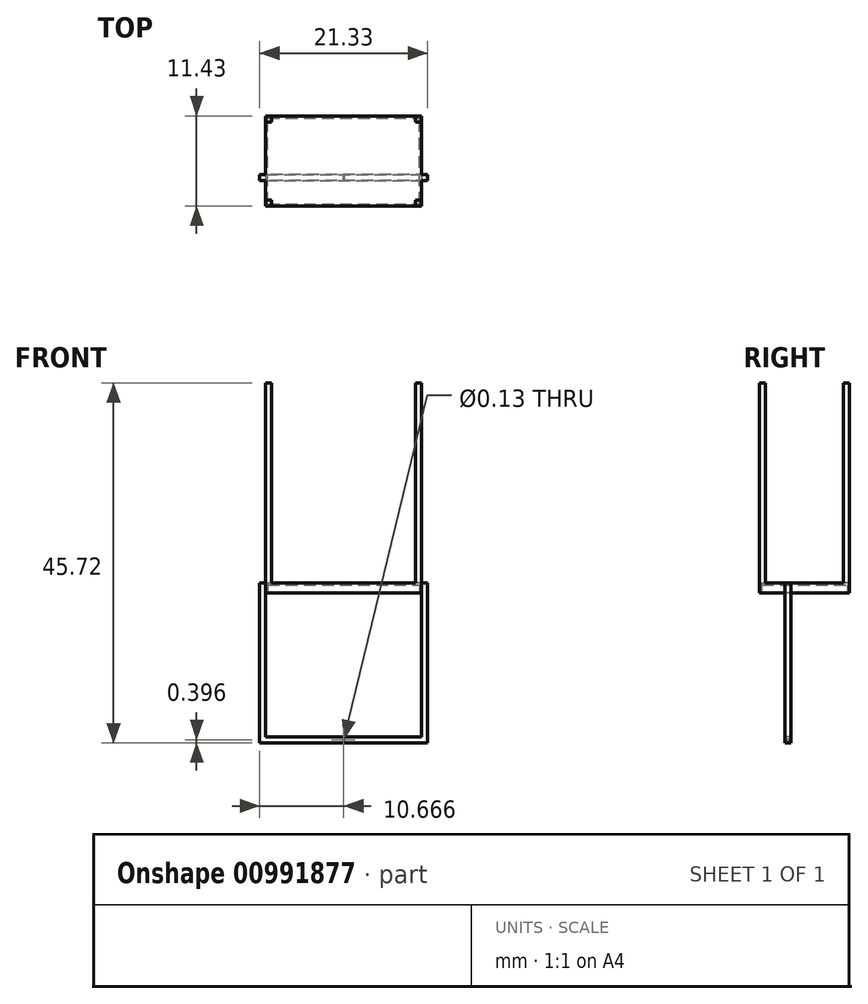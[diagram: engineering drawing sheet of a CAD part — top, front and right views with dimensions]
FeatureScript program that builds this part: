
annotation { "Feature Type Name" : "Feature", "Feature Type Description" : "" }
export const myFeature = defineFeature(function(context is Context, id is Id, definition is map)
    precondition{}
    {
        {
            var Q0;
            Q0=qCreatedBy(makeId("Top.planeOp"),FACE);
            var sketch = newSketch(context, id + "F0", { "sketchPlane" : qUnion([Q0])});
            skLineSegment(sketch, "E0.bottom", {"start": v(0, 0) * mm, "end": v(19.81, 0) * mm});
            skLineSegment(sketch, "E0.top", {"start": v(0, 11.43) * mm, "end": v(19.81, 11.43) * mm});
            skLineSegment(sketch, "E0.left", {"start": v(0, 0) * mm, "end": v(0, 11.43) * mm});
            skLineSegment(sketch, "E0.right", {"start": v(19.81, 0) * mm, "end": v(19.81, 11.43) * mm});
            skSolve(sketch);
        }
        {
            var Q0;
            Q0=makeQuery(id+"F0.imprint","IMPRINT",FACE,{"disambiguationData":[TD([[makeQuery(id+"F0.imprint","IMPRINT",EDGE,{"derivedFrom":sQuery(id+"F0.wireOp",EDGE,"E0.bottom")}),1.0]])]});
            extrude(context, id + "F1", {"entities" : qUnion([Q0]), "depth" : 1.27 * mm, "offsetDistance" : 25.4 * mm});
        }
        {
            var Q0;
            Q0=makeQuery(id+"F1.opExtrude","CAP_FACE",FACE,{"disambiguationData":[OSD([sQuery(id+"F0.wireOp",EDGE,"E0.bottom"),sQuery(id+"F0.wireOp",EDGE,"E0.top"),sQuery(id+"F0.wireOp",EDGE,"E0.left"),sQuery(id+"F0.wireOp",EDGE,"E0.right")])],"isStart":true});
            shell(context, id + "F2", {"entities" : qUnion([Q0]), "thickness" : 0.25 * mm});
        }
        {
            var Q0;
            Q0=makeQuery(id+"F1.opExtrude","CAP_FACE",FACE,{"disambiguationData":[OSD([sQuery(id+"F0.wireOp",EDGE,"E0.bottom"),sQuery(id+"F0.wireOp",EDGE,"E0.top"),sQuery(id+"F0.wireOp",EDGE,"E0.left"),sQuery(id+"F0.wireOp",EDGE,"E0.right")])],"isStart":false});
            var sketch = newSketch(context, id + "F3", { "sketchPlane" : qUnion([Q0])});
            skLineSegment(sketch, "E1.bottom", {"start": v(19.81, 0) * mm, "end": v(19.05, 0) * mm});
            skLineSegment(sketch, "E1.top", {"start": v(19.81, 0.76) * mm, "end": v(19.05, 0.76) * mm});
            skLineSegment(sketch, "E1.left", {"start": v(19.81, 0) * mm, "end": v(19.81, 0.76) * mm});
            skLineSegment(sketch, "E1.right", {"start": v(19.05, 0) * mm, "end": v(19.05, 0.76) * mm});
            skLineSegment(sketch, "E2.bottom", {"start": v(19.81, 11.43) * mm, "end": v(19.05, 11.43) * mm});
            skLineSegment(sketch, "E2.top", {"start": v(19.81, 10.67) * mm, "end": v(19.05, 10.67) * mm});
            skLineSegment(sketch, "E2.left", {"start": v(19.81, 11.43) * mm, "end": v(19.81, 10.67) * mm});
            skLineSegment(sketch, "E2.right", {"start": v(19.05, 11.43) * mm, "end": v(19.05, 10.67) * mm});
            skLineSegment(sketch, "E3.bottom", {"start": v(0, 11.43) * mm, "end": v(0.76, 11.43) * mm});
            skLineSegment(sketch, "E3.top", {"start": v(0, 10.67) * mm, "end": v(0.76, 10.67) * mm});
            skLineSegment(sketch, "E3.left", {"start": v(0, 11.43) * mm, "end": v(0, 10.67) * mm});
            skLineSegment(sketch, "E3.right", {"start": v(0.76, 11.43) * mm, "end": v(0.76, 10.67) * mm});
            skLineSegment(sketch, "E4.bottom", {"start": v(0, 0) * mm, "end": v(0.76, 0) * mm});
            skLineSegment(sketch, "E4.top", {"start": v(0, 0.76) * mm, "end": v(0.76, 0.76) * mm});
            skLineSegment(sketch, "E4.left", {"start": v(0, 0) * mm, "end": v(0, 0.76) * mm});
            skLineSegment(sketch, "E4.right", {"start": v(0.76, 0) * mm, "end": v(0.76, 0.76) * mm});
            skSolve(sketch);
        }
        {
            var Q0;
            Q0 = qSketchRegion(id + "F3", true);
            extrude(context, id + "F4", {"entities" : qUnion([Q0]), "operationType" : NewBodyOperationType.ADD, "depth" : 25.4 * mm, "offsetDistance" : 25.4 * mm});
        }
        {
            var Q0;
            Q0=makeQuery(id+"F4.boolean.opBoolean","MERGE",FACE,{"derivedFrom":[makeQuery(id+"F1.opExtrude","SWEPT_FACE",FACE,{"disambiguationData":[OSD([sQuery(id+"F0.wireOp",EDGE,"E0.right")])]}),makeQuery(id+"F4.opExtrude","SWEPT_FACE",FACE,{"disambiguationData":[OSD([sQuery(id+"F3.wireOp",EDGE,"E1.left")])]}),makeQuery(id+"F4.opExtrude","SWEPT_FACE",FACE,{"disambiguationData":[OSD([sQuery(id+"F3.wireOp",EDGE,"E2.left")])]})]});
            var sketch = newSketch(context, id + "F5", { "sketchPlane" : qUnion([Q0])});
            skLineSegment(sketch, "E5.bottom", {"start": v(4, 0) * mm, "end": v(3.23, 0) * mm});
            skLineSegment(sketch, "E5.top", {"start": v(4, 1.27) * mm, "end": v(3.23, 1.27) * mm});
            skLineSegment(sketch, "E5.left", {"start": v(4, 0) * mm, "end": v(4, 1.27) * mm});
            skLineSegment(sketch, "E5.right", {"start": v(3.23, 0) * mm, "end": v(3.23, 1.27) * mm});
            skSolve(sketch);
        }
        {
            var Q0;
            Q0 = qSketchRegion(id + "F5", true);
            extrude(context, id + "F6", {"entities" : qUnion([Q0]), "operationType" : NewBodyOperationType.ADD, "depth" : 0.76 * mm, "offsetDistance" : 25.4 * mm});
        }
        {
            var Q0;
            Q0=makeQuery(id+"F6.boolean.opBoolean","MERGE",FACE,{"derivedFrom":[makeQuery(id+"F1.opExtrude","CAP_FACE",FACE,{"disambiguationData":[OSD([sQuery(id+"F0.wireOp",EDGE,"E0.bottom"),sQuery(id+"F0.wireOp",EDGE,"E0.top"),sQuery(id+"F0.wireOp",EDGE,"E0.left"),sQuery(id+"F0.wireOp",EDGE,"E0.right")])],"isStart":true}),makeQuery(id+"F6.opExtrude","SWEPT_FACE",FACE,{"disambiguationData":[OSD([sQuery(id+"F5.wireOp",EDGE,"E5.bottom")])]})]});
            var sketch = newSketch(context, id + "F7", { "sketchPlane" : qUnion([Q0])});
            skLineSegment(sketch, "E6.bottom", {"start": v(20.57, -4) * mm, "end": v(19.81, -4) * mm});
            skLineSegment(sketch, "E6.top", {"start": v(20.57, -3.23) * mm, "end": v(19.81, -3.23) * mm});
            skLineSegment(sketch, "E6.left", {"start": v(20.57, -4) * mm, "end": v(20.57, -3.23) * mm});
            skLineSegment(sketch, "E6.right", {"start": v(19.81, -4) * mm, "end": v(19.81, -3.23) * mm});
            skSolve(sketch);
        }
        {
            var Q0;
            Q0 = qSketchRegion(id + "F7", true);
            extrude(context, id + "F8", {"entities" : qUnion([Q0]), "operationType" : NewBodyOperationType.ADD, "depth" : 19.05 * mm, "offsetDistance" : 25.4 * mm});
        }
        {
            var Q0;
            Q0=makeQuery(id+"F8.opExtrude","SWEPT_FACE",FACE,{"disambiguationData":[OSD([sQuery(id+"F7.wireOp",EDGE,"E6.right")])]});
            var sketch = newSketch(context, id + "F9", { "sketchPlane" : qUnion([Q0])});
            skLineSegment(sketch, "E7.bottom", {"start": v(-4, -19.05) * mm, "end": v(-3.23, -19.05) * mm});
            skLineSegment(sketch, "E7.top", {"start": v(-4, -18.29) * mm, "end": v(-3.23, -18.29) * mm});
            skLineSegment(sketch, "E7.left", {"start": v(-4, -19.05) * mm, "end": v(-4, -18.29) * mm});
            skLineSegment(sketch, "E7.right", {"start": v(-3.23, -19.05) * mm, "end": v(-3.23, -18.29) * mm});
            skSolve(sketch);
        }
        {
            var Q0;
            Q0 = qSketchRegion(id + "F9", true);
            extrude(context, id + "F10", {"entities" : qUnion([Q0]), "operationType" : NewBodyOperationType.ADD, "depth" : 20.57 * mm, "offsetDistance" : 25.4 * mm});
        }
        {
            var Q0;
            Q0=makeQuery(id+"F10.opExtrude","SWEPT_FACE",FACE,{"disambiguationData":[OSD([sQuery(id+"F9.wireOp",EDGE,"E7.top")])]});
            var sketch = newSketch(context, id + "F11", { "sketchPlane" : qUnion([Q0])});
            skLineSegment(sketch, "E8.bottom", {"start": v(-0.76, 4) * mm, "end": v(0, 4) * mm});
            skLineSegment(sketch, "E8.top", {"start": v(-0.76, 3.23) * mm, "end": v(0, 3.23) * mm});
            skLineSegment(sketch, "E8.left", {"start": v(-0.76, 4) * mm, "end": v(-0.76, 3.23) * mm});
            skLineSegment(sketch, "E8.right", {"start": v(0, 4) * mm, "end": v(0, 3.23) * mm});
            skSolve(sketch);
        }
        {
            var Q0;
            Q0 = qSketchRegion(id + "F11", true);
            extrude(context, id + "F12", {"entities" : qUnion([Q0]), "operationType" : NewBodyOperationType.ADD, "depth" : 19.56 * mm, "offsetDistance" : 25.4 * mm});
        }
        {
            var Q0;
            Q0=makeQuery(id+"F12.boolean.opBoolean","MERGE",FACE,{"derivedFrom":[makeQuery(id+"F10.boolean.opBoolean","MERGE",FACE,{"derivedFrom":[makeQuery(id+"F8.boolean.opBoolean","MERGE",FACE,{"derivedFrom":[makeQuery(id+"F6.opExtrude","SWEPT_FACE",FACE,{"disambiguationData":[OSD([sQuery(id+"F5.wireOp",EDGE,"E5.right")])]}),makeQuery(id+"F8.opExtrude","SWEPT_FACE",FACE,{"disambiguationData":[OSD([sQuery(id+"F7.wireOp",EDGE,"E6.top")])]})]}),makeQuery(id+"F10.opExtrude","SWEPT_FACE",FACE,{"disambiguationData":[OSD([sQuery(id+"F9.wireOp",EDGE,"E7.right")])]})]}),makeQuery(id+"F12.opExtrude","SWEPT_FACE",FACE,{"disambiguationData":[OSD([sQuery(id+"F11.wireOp",EDGE,"E8.top")])]})]});
            var sketch = newSketch(context, id + "F13", { "sketchPlane" : qUnion([Q0])});
            skCircle(sketch, "E9", {"center": v(9.9, -18.65) * mm, "radius": 0.06 * mm});
            skPoint(sketch, "E9.centerSnap0", {"position": v(9.9, -19.05) * mm});
            skSolve(sketch);
        }
        {
            var Q0;
            Q0=sQuery(id+"F13.wireOp",VERTEX,"E9.center");
            var Q1;
            Q1=makeQuery(id+"F1.opExtrude","SWEPT_BODY",BODY,{"disambiguationData":[OSD([sQuery(id+"F0.wireOp",EDGE,"E0.bottom"),sQuery(id+"F0.wireOp",EDGE,"E0.top"),sQuery(id+"F0.wireOp",EDGE,"E0.left"),sQuery(id+"F0.wireOp",EDGE,"E0.right")])]});
            hole(context, id + "F14", {"style" : HoleStyle.SIMPLE, "endStyle" : HoleEndStyle.THROUGH, "holeDiameter" : 0.13 * mm, "majorDiameter" : 6.35 * mm, "isTappedThrough" : true, "tappedDepth" : 12.7 * mm, "tapClearance" : 3, "locations" : qUnion([Q0]), "scope" : qUnion([Q1])});
        }
    });
